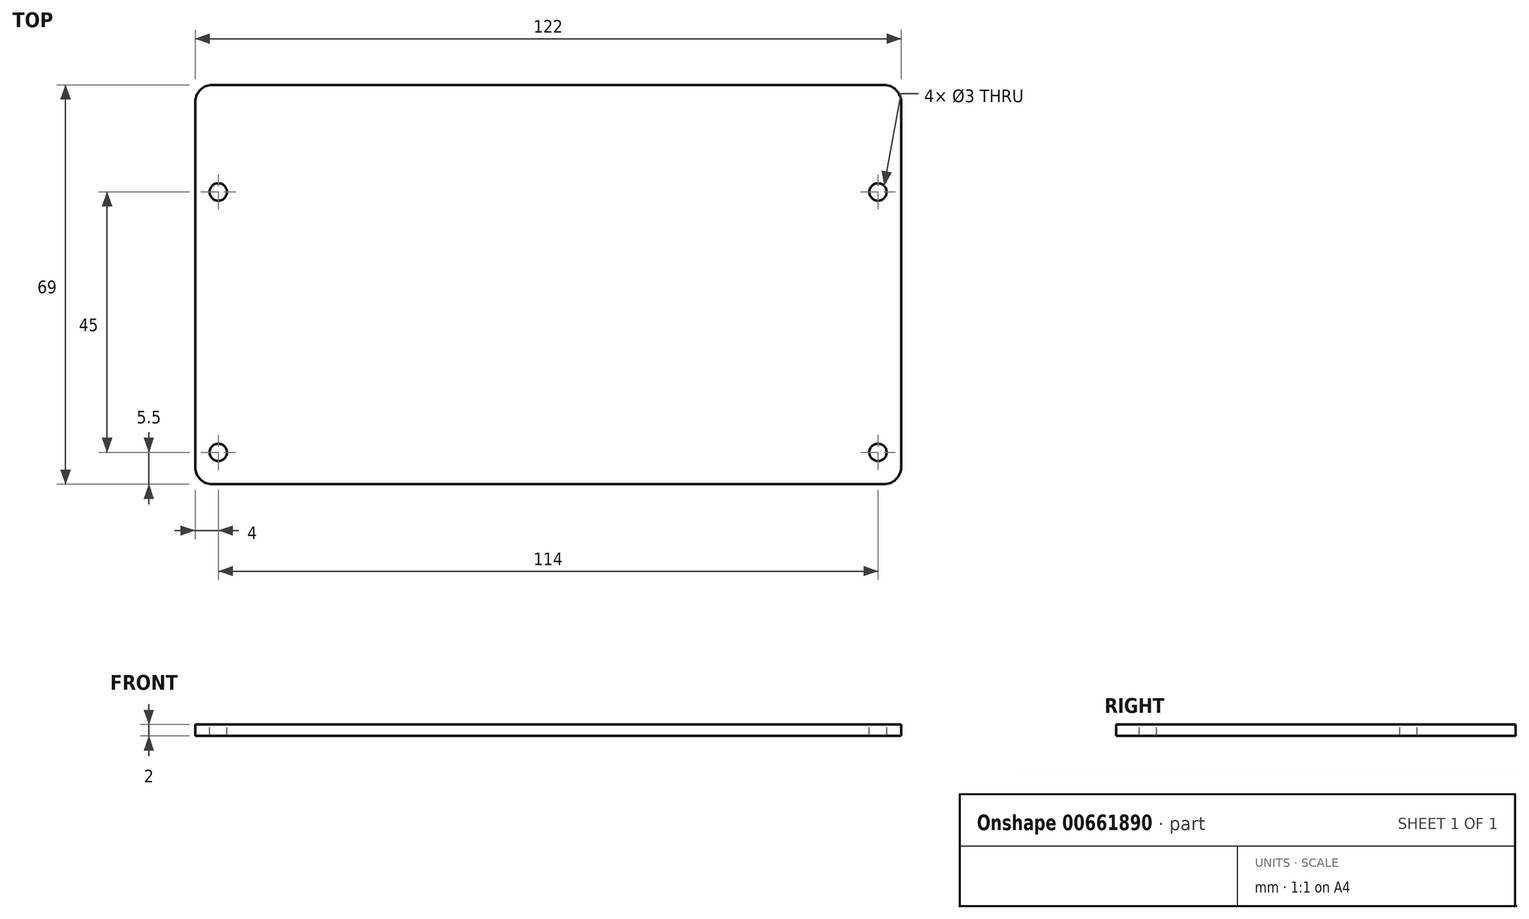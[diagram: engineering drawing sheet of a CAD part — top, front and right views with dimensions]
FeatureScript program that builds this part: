
annotation { "Feature Type Name" : "Feature", "Feature Type Description" : "" }
export const myFeature = defineFeature(function(context is Context, id is Id, definition is map)
    precondition{}
    {
        {
            var Q0;
            Q0=qCreatedBy(makeId("Top.planeOp"),FACE);
            var sketch = newSketch(context, id + "F0", { "sketchPlane" : qUnion([Q0])});
            skLineSegment(sketch, "E0.bottom", {"start": v(-61, 28) * mm, "end": v(61, 28) * mm});
            skLineSegment(sketch, "E0.top", {"start": v(-61, -28) * mm, "end": v(61, -28) * mm});
            skLineSegment(sketch, "E0.left", {"start": v(-61, 28) * mm, "end": v(-61, -28) * mm});
            skLineSegment(sketch, "E0.right", {"start": v(61, 28) * mm, "end": v(61, -28) * mm});
            skPoint(sketch, "E0.middle", {"position": v(0, 0) * mm});
            skLineSegment(sketch, "E1", {"start": v(0, -28) * mm, "end": v(0, 28) * mm, "construction": true});
            skLineSegment(sketch, "E2.bottom", {"start": v(-55.5, -17) * mm, "end": v(55.5, -17) * mm, "construction": true});
            skLineSegment(sketch, "E2.top", {"start": v(-55.5, 17) * mm, "end": v(55.5, 17) * mm, "construction": true});
            skLineSegment(sketch, "E2.left", {"start": v(-55.5, -17) * mm, "end": v(-55.5, 17) * mm, "construction": true});
            skLineSegment(sketch, "E2.right", {"start": v(55.5, -17) * mm, "end": v(55.5, 17) * mm, "construction": true});
            skLineSegment(sketch, "E3", {"start": v(-55.5, 0) * mm, "end": v(55.5, 0) * mm, "construction": true});
            skCircle(sketch, "E4", {"center": v(-57, 22.5) * mm, "radius": 1.5 * mm});
            skCircle(sketch, "E5.MirrorC", {"center": v(-57, -22.5) * mm, "radius": 1.5 * mm});
            skCircle(sketch, "E6.MirrorC", {"center": v(57, 22.5) * mm, "radius": 1.5 * mm});
            skCircle(sketch, "E7.MirrorC", {"center": v(57, -22.5) * mm, "radius": 1.5 * mm});
            skLineSegment(sketch, "E8.bottom", {"start": v(-57, 22.5) * mm, "end": v(57, 22.5) * mm, "construction": true});
            skLineSegment(sketch, "E8.top", {"start": v(-57, -22.5) * mm, "end": v(57, -22.5) * mm, "construction": true});
            skLineSegment(sketch, "E8.left", {"start": v(-57, 22.5) * mm, "end": v(-57, -22.5) * mm, "construction": true});
            skLineSegment(sketch, "E8.right", {"start": v(57, 22.5) * mm, "end": v(57, -22.5) * mm, "construction": true});
            skCircle(sketch, "E9", {"center": v(-55.5, 0) * mm, "radius": 2.5 * mm, "construction": true});
            skCircle(sketch, "E10", {"center": v(55.5, 0) * mm, "radius": 2.5 * mm, "construction": true});
            skLineSegment(sketch, "E11", {"start": v(-57, 22.5) * mm, "end": v(-61, 22.5) * mm, "construction": true});
            skLineSegment(sketch, "E12", {"start": v(-57, 22.5) * mm, "end": v(-57, 28) * mm, "construction": true});
            skSolve(sketch);
        }
        {
            var Q0;
            Q0 = qSketchRegion(id + "F0", true);
            extrude(context, id + "F1", {"entities" : qUnion([Q0]), "oppositeDirection" : true, "depth" : 2 * mm, "offsetDistance" : 25 * mm});
        }
        {
            var Q0;
            Q0=makeQuery(id+"F1.opExtrude","SWEPT_FACE",FACE,{"disambiguationData":[OSD([sQuery(id+"F0.wireOp",EDGE,"E0.bottom")])]});
            extrude(context, id + "F2", {"entities" : qUnion([Q0]), "operationType" : NewBodyOperationType.ADD, "depth" : 13 * mm, "offsetDistance" : 25 * mm});
        }
        {
            var Q0;
            {var subQ0=sQuery(id+"F0.wireOp",EDGE,"E0.bottom");Q0=makeQuery(id+"F2.boolean.opBoolean","MERGE",FACE,{"derivedFrom":[makeQuery(id+"F1.opExtrude","CAP_FACE",FACE,{"disambiguationData":[OSD([subQ0,sQuery(id+"F0.wireOp",EDGE,"E0.top"),sQuery(id+"F0.wireOp",EDGE,"E0.left"),sQuery(id+"F0.wireOp",EDGE,"E0.right"),sQuery(id+"F0.wireOp",EDGE,"E4"),sQuery(id+"F0.wireOp",EDGE,"E5.MirrorC"),sQuery(id+"F0.wireOp",EDGE,"E6.MirrorC"),sQuery(id+"F0.wireOp",EDGE,"E7.MirrorC")])],"isStart":true}),makeQuery(id+"F2.opExtrude","SWEPT_FACE",FACE,{"disambiguationData":[OSD([subQ0]),TDD([makeQuery(id+"F1.opExtrude","CAP_EDGE",EDGE,{"disambiguationData":[OSD([subQ0])],"isStart":true})])]})]});}
            var sketch = newSketch(context, id + "F3", { "sketchPlane" : qUnion([Q0])});
            skLineSegment(sketch, "E13", {"start": v(-61, -25.4) * mm, "end": v(61, -25.4) * mm, "construction": true});
            skCircle(sketch, "E14", {"center": v(-41, -25.4) * mm, "radius": 6 * mm, "construction": true});
            skCircle(sketch, "E15", {"center": v(-25, -25.4) * mm, "radius": 6 * mm, "construction": true});
            skCircle(sketch, "E16", {"center": v(37, -25.4) * mm, "radius": 6 * mm, "construction": true});
            skLineSegment(sketch, "E17", {"start": v(6, -28) * mm, "end": v(6, -22.5) * mm, "construction": true});
            skCircle(sketch, "E18", {"center": v(6, -22.5) * mm, "radius": 3.5 * mm, "construction": true});
            skSolve(sketch);
        }
        {
            var Q0;
            Q0=makeQuery(id+"F1.opExtrude","SWEPT_EDGE",EDGE,{"disambiguationData":[OSD([sQuery(id+"F0.wireOp",EDGE,"E0.top"),sQuery(id+"F0.wireOp",EDGE,"E0.left")])]});
            var Q1;
            Q1=makeQuery(id+"F1.opExtrude","SWEPT_EDGE",EDGE,{"disambiguationData":[OSD([sQuery(id+"F0.wireOp",EDGE,"E0.top"),sQuery(id+"F0.wireOp",EDGE,"E0.right")])]});
            var Q2;
            Q2=makeQuery(id+"F2.opExtrude","CAP_EDGE",EDGE,{"disambiguationData":[OSD([sQuery(id+"F0.wireOp",EDGE,"E0.bottom"),sQuery(id+"F0.wireOp",EDGE,"E0.right")])],"isStart":false});
            var Q3;
            Q3=makeQuery(id+"F2.opExtrude","CAP_EDGE",EDGE,{"disambiguationData":[OSD([sQuery(id+"F0.wireOp",EDGE,"E0.bottom"),sQuery(id+"F0.wireOp",EDGE,"E0.left")])],"isStart":false});
            fillet(context, id + "F4", {"entities" : qUnion([Q0, Q1, Q2, Q3]), "radius" : 3 * mm, "tangentPropagation" : true, "allowEdgeOverflow" : false});
        }
        {
            var Q0;
            Q0=makeQuery(id+"F3.imprint","IMPRINT",FACE,{"disambiguationData":[TD([[makeQuery(id+"F3.imprint","IMPRINT",EDGE,{"derivedFrom":makeQuery(id+"F1.opExtrude","CAP_EDGE",EDGE,{"disambiguationData":[OSD([sQuery(id+"F0.wireOp",EDGE,"E0.top")])],"isStart":true})}),1.0]])]});
            var sketch = newSketch(context, id + "F5", { "sketchPlane" : qUnion([Q0])});
            skLineSegment(sketch, "E19", {"start": v(31, 33) * mm, "end": v(31, 41) * mm, "construction": true});
            skCircle(sketch, "E20", {"center": v(31, 33) * mm, "radius": 6 * mm, "construction": true});
            skSolve(sketch);
        }
    });
